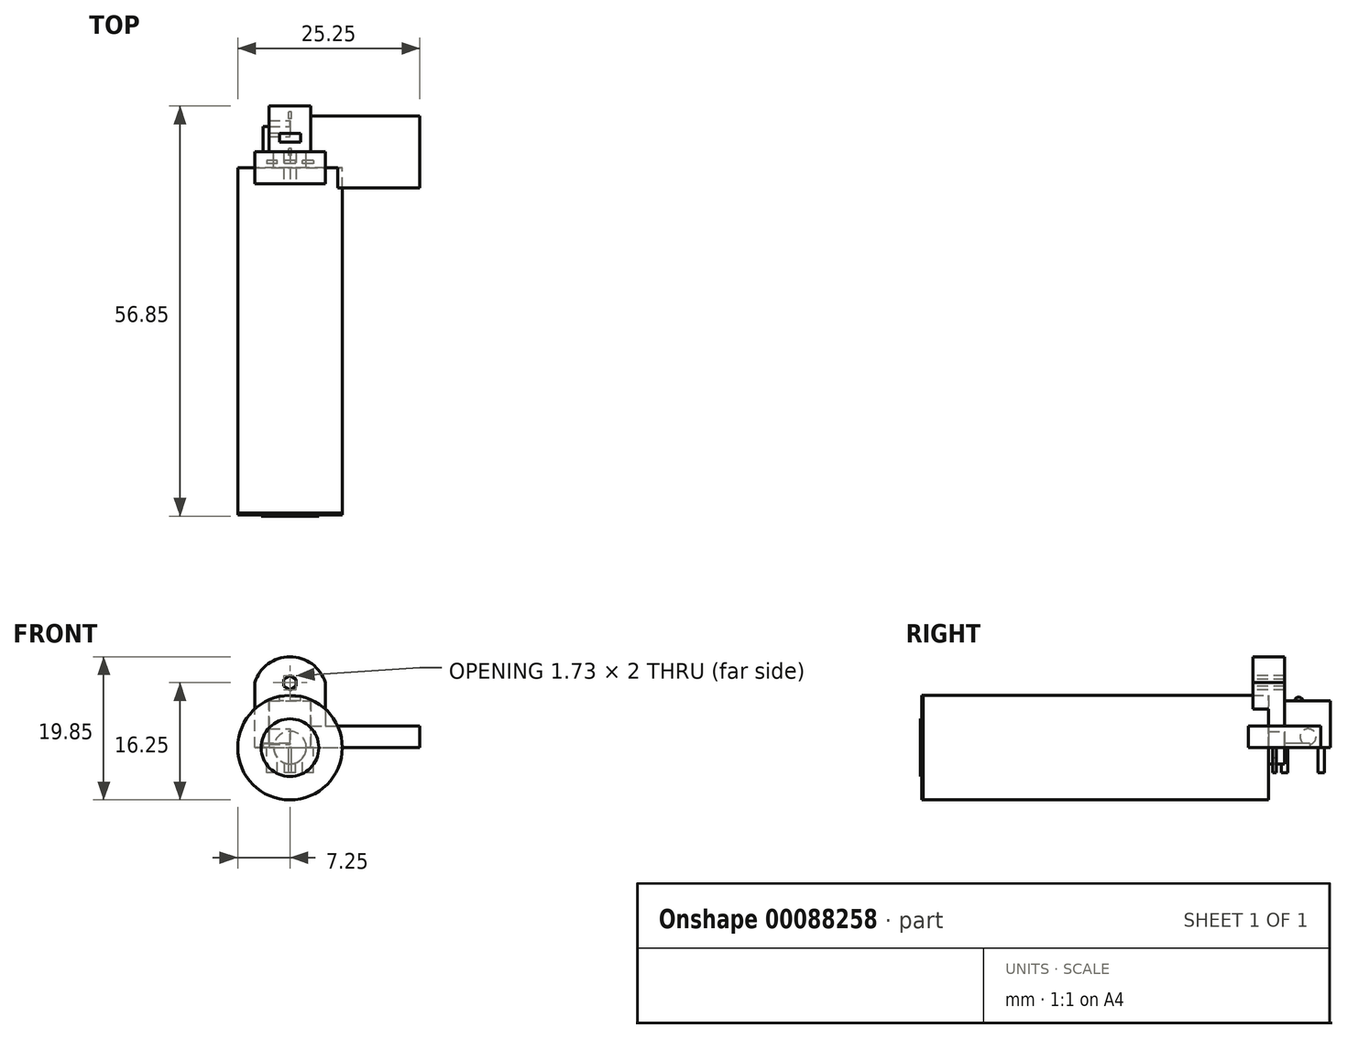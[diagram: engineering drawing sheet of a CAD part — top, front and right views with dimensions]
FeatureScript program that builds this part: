
annotation { "Feature Type Name" : "Feature", "Feature Type Description" : "" }
export const myFeature = defineFeature(function(context is Context, id is Id, definition is map)
    precondition{}
    {
        {
            var Q0;
            Q0=qCreatedBy(makeId("Top.planeOp"),FACE);
            var sketch = newSketch(context, id + "F0", { "sketchPlane" : qUnion([Q0])});
            skLineSegment(sketch, "E0.bottom", {"start": v(-2.9, 6.35) * mm, "end": v(2.9, 6.35) * mm});
            skLineSegment(sketch, "E0.top", {"start": v(-2.9, -6.35) * mm, "end": v(2.9, -6.35) * mm});
            skLineSegment(sketch, "E0.left", {"start": v(-2.9, 6.35) * mm, "end": v(-2.9, -6.35) * mm});
            skLineSegment(sketch, "E0.right", {"start": v(2.9, 6.35) * mm, "end": v(2.9, -6.35) * mm});
            skLineSegment(sketch, "E1", {"start": v(0, 9.5) * mm, "end": v(0, 7.35) * mm, "construction": true});
            skLineSegment(sketch, "E2", {"start": v(6.86, 0) * mm, "end": v(4.55, 0) * mm, "construction": true});
            skSolve(sketch);
        }
        {
            var Q0;
            Q0=qSketchRegion(id+"F0",true);
            extrude(context, id + "F1", {"entities" : qUnion([Q0]), "depth" : 6.5 * mm});
        }
        {
            var Q0;
            Q0=makeQuery(id+"F1.opExtrude","CAP_FACE",FACE,{"disambiguationData":[OSD([sQuery(id+"F0.wireOp",EDGE,"E0.bottom"),sQuery(id+"F0.wireOp",EDGE,"E0.top"),sQuery(id+"F0.wireOp",EDGE,"E0.left"),sQuery(id+"F0.wireOp",EDGE,"E0.right")])],"isStart":true});
            var sketch = newSketch(context, id + "F2", { "sketchPlane" : qUnion([Q0])});
            skLineSegment(sketch, "E3.bottom", {"start": v(0.2, 5.53) * mm, "end": v(-0.2, 5.53) * mm});
            skLineSegment(sketch, "E3.top", {"start": v(0.2, 4.63) * mm, "end": v(-0.2, 4.63) * mm});
            skLineSegment(sketch, "E3.left", {"start": v(0.2, 5.53) * mm, "end": v(0.2, 4.63) * mm});
            skLineSegment(sketch, "E3.right", {"start": v(-0.2, 5.53) * mm, "end": v(-0.2, 4.63) * mm});
            skLineSegment(sketch, "E4", {"start": v(1.77, 5.08) * mm, "end": v(0.77, 5.08) * mm, "construction": true});
            skLineSegment(sketch, "E5", {"start": v(0, -0.8) * mm, "end": v(0, -1.46) * mm, "construction": true});
            skLineSegment(sketch, "E6.0.1.0", {"start": v(-0.2, 0.45) * mm, "end": v(-0.2, -0.45) * mm});
            skLineSegment(sketch, "E6.0.1.1", {"start": v(0.2, 0.45) * mm, "end": v(0.2, -0.45) * mm});
            skLineSegment(sketch, "E6.0.1.2", {"start": v(0.2, -0.45) * mm, "end": v(-0.2, -0.45) * mm});
            skLineSegment(sketch, "E6.0.1.3", {"start": v(0.2, 0.45) * mm, "end": v(-0.2, 0.45) * mm});
            skLineSegment(sketch, "E6.0.2.0", {"start": v(-0.2, -4.63) * mm, "end": v(-0.2, -5.53) * mm});
            skLineSegment(sketch, "E6.0.2.1", {"start": v(0.2, -4.63) * mm, "end": v(0.2, -5.53) * mm});
            skLineSegment(sketch, "E6.0.2.2", {"start": v(0.2, -5.53) * mm, "end": v(-0.2, -5.53) * mm});
            skLineSegment(sketch, "E6.0.2.3", {"start": v(0.2, -4.63) * mm, "end": v(-0.2, -4.63) * mm});
            skLineSegment(sketch, "E6.direction1", {"start": v(-0.2, 4.63) * mm, "end": v(24.8, 4.63) * mm, "construction": true});
            skLineSegment(sketch, "E6.direction2", {"start": v(-0.2, 4.63) * mm, "end": v(-0.2, -0.45) * mm, "construction": true});
            skSolve(sketch);
        }
        {
            var Q0;
            Q0=qSketchRegion(id+"F2",true);
            extrude(context, id + "F3", {"entities" : qUnion([Q0]), "operationType" : NewBodyOperationType.ADD, "depth" : 3.5 * mm});
        }
        {
            var Q0;
            Q0=qCreatedBy(makeId("Right.planeOp"),FACE);
            var sketch = newSketch(context, id + "F4", { "sketchPlane" : qUnion([Q0])});
            skCircle(sketch, "E7", {"center": v(1.95, 6.4) * mm, "radius": 0.6 * mm});
            skSolve(sketch);
        }
        {
            var Q0;
            Q0=qSketchRegion(id+"F4",true);
            extrude(context, id + "F5", {"entities" : qUnion([Q0]), "operationType" : NewBodyOperationType.ADD, "endBound" : BoundingType.SYMMETRIC, "depth" : 2.9 * mm});
        }
        {
            var Q0;
            Q0=makeQuery(id+"F1.opExtrude","SWEPT_FACE",FACE,{"disambiguationData":[OSD([sQuery(id+"F0.wireOp",EDGE,"E0.right")])]});
            var sketch = newSketch(context, id + "F6", { "sketchPlane" : qUnion([Q0])});
            skCircle(sketch, "E8", {"center": v(3.25, 1.5) * mm, "radius": 1.1 * mm});
            skCircle(sketch, "E9.1.0.0", {"center": v(-3.75, 1.5) * mm, "radius": 1.1 * mm});
            skLineSegment(sketch, "E9.direction1", {"start": v(3.25, 1.5) * mm, "end": v(-3.75, 1.5) * mm, "construction": true});
            skSolve(sketch);
        }
        {
            var Q0;
            Q0=qSketchRegion(id+"F6",true);
            var Q1;
            Q1=makeQuery(id+"F1.opExtrude","SWEPT_FACE",FACE,{"disambiguationData":[OSD([sQuery(id+"F0.wireOp",EDGE,"E0.left")])]});
            extrude(context, id + "F7", {"entities" : qUnion([Q0]), "operationType" : NewBodyOperationType.REMOVE, "endBound" : BoundingType.UP_TO_SURFACE, "oppositeDirection" : true, "endBoundEntityFace" : qUnion([Q1]), "depth" : 25 * mm});
        }
        {
            var Q0;
            Q0=qCreatedBy(makeId("Top.planeOp"),FACE);
            var sketch = newSketch(context, id + "F8", { "sketchPlane" : qUnion([Q0])});
            skLineSegment(sketch, "E10", {"start": v(0, 17.78) * mm, "end": v(0, 11.28) * mm, "construction": true});
            skLineSegment(sketch, "E11", {"start": v(0, 0) * mm, "end": v(2.25, 0) * mm});
            skLineSegment(sketch, "E12", {"start": v(2.25, 0) * mm, "end": v(2.25, -2.2) * mm});
            skLineSegment(sketch, "E13", {"start": v(2.25, -2.2) * mm, "end": v(7.25, -2.2) * mm});
            skLineSegment(sketch, "E14", {"start": v(7.25, -2.2) * mm, "end": v(7.25, -50.3) * mm});
            skLineSegment(sketch, "E15", {"start": v(7.25, -50.3) * mm, "end": v(4, -50.3) * mm});
            skLineSegment(sketch, "E16", {"start": v(4, -50.3) * mm, "end": v(4, -50.5) * mm});
            skLineSegment(sketch, "E17", {"start": v(4, -50.5) * mm, "end": v(0, -50.5) * mm});
            skLineSegment(sketch, "E18", {"start": v(0, -50.5) * mm, "end": v(0, 0) * mm});
            skSolve(sketch);
        }
        {
            var Q0;
            Q0=qSketchRegion(id+"F8",true);
            var Q1;
            Q1=sQuery(id+"F8.wireOp",EDGE,"E10");
            revolve(context, id + "F9", {"entities" : qUnion([Q0]), "axis" : qUnion([Q1]), "revolveType" : RevolveType.FULL});
        }
        {
            var Q0;
            Q0=qCreatedBy(makeId("Top.planeOp"),FACE);
            var sketch = newSketch(context, id + "F10", { "sketchPlane" : qUnion([Q0])});
            skLineSegment(sketch, "E19.rect.bottom", {"start": v(0, 5) * mm, "end": v(18, 5) * mm});
            skLineSegment(sketch, "E19.rect.top", {"start": v(0, -5) * mm, "end": v(18, -5) * mm});
            skLineSegment(sketch, "E19.rect.left", {"start": v(0, 5) * mm, "end": v(0, -5) * mm});
            skLineSegment(sketch, "E19.rect.right", {"start": v(18, 5) * mm, "end": v(18, -5) * mm});
            skPoint(sketch, "E19.rect.middle", {"position": v(9, 0) * mm});
            skSolve(sketch);
        }
        {
            var Q0;
            Q0=qSketchRegion(id+"F10",true);
            extrude(context, id + "F11", {"entities" : qUnion([Q0]), "depth" : 3 * mm});
        }
        {
            var Q0;
            Q0=qCreatedBy(makeId("Top.planeOp"),FACE);
            var sketch = newSketch(context, id + "F12", { "sketchPlane" : qUnion([Q0])});
            skLineSegment(sketch, "E20.rect.bottom", {"start": v(3.75, 3.5) * mm, "end": v(-3.75, 3.5) * mm});
            skLineSegment(sketch, "E20.rect.top", {"start": v(3.75, -3.5) * mm, "end": v(-3.75, -3.5) * mm});
            skLineSegment(sketch, "E20.rect.left", {"start": v(3.75, 3.5) * mm, "end": v(3.75, -3.5) * mm});
            skLineSegment(sketch, "E20.rect.right", {"start": v(-3.75, 3.5) * mm, "end": v(-3.75, -3.5) * mm});
            skPoint(sketch, "E20.rect.middle", {"position": v(0, 0) * mm});
            skSolve(sketch);
        }
        {
            var Q0;
            Q0=qSketchRegion(id+"F12",true);
            extrude(context, id + "F13", {"entities" : qUnion([Q0]), "depth" : 0.6 * mm});
        }
        {
            var Q0;
            Q0=qCreatedBy(makeId("Front.planeOp"),FACE);
            var sketch = newSketch(context, id + "F14", { "sketchPlane" : qUnion([Q0])});
            skLineSegment(sketch, "E21", {"start": v(0, 14.23) * mm, "end": v(0, 3.29) * mm, "construction": true});
            skLineSegment(sketch, "E22", {"start": v(4.9, 0) * mm, "end": v(-4.9, 0) * mm});
            skLineSegment(sketch, "E23", {"start": v(-4.9, 0) * mm, "end": v(-4.9, 9) * mm});
            skLineSegment(sketch, "E24", {"start": v(-4.9, 9) * mm, "end": v(4.9, 9) * mm, "construction": true});
            skLineSegment(sketch, "E25", {"start": v(4.9, 9) * mm, "end": v(4.9, 0) * mm});
            skArc(sketch, "E26", {"start": v(4.9, 9) * mm, "mid": v(0, 12.6) * mm, "end": v(-4.9, 9) * mm});
            skPoint(sketch, "E27", {"position": v(0, 9) * mm});
            skSolve(sketch);
        }
        {
            var Q0;
            Q0=qSketchRegion(id+"F14",true);
            extrude(context, id + "F15", {"entities" : qUnion([Q0]), "depth" : 4.4 * mm});
        }
        {
            var Q0;
            Q0=makeQuery(id+"F15.opExtrude","CAP_FACE",FACE,{"disambiguationData":[OSD([sQuery(id+"F14.wireOp",EDGE,"E22"),sQuery(id+"F14.wireOp",EDGE,"E23"),sQuery(id+"F14.wireOp",EDGE,"E25"),sQuery(id+"F14.wireOp",EDGE,"E26")])],"isStart":false});
            var sketch = newSketch(context, id + "F16", { "sketchPlane" : qUnion([Q0])});
            skPoint(sketch, "E28.0", {"position": v(0, 9) * mm});
            skCircle(sketch, "E29.cCircle", {"center": v(0, 9) * mm, "radius": 0.87 * mm, "construction": true});
            skLineSegment(sketch, "E29.0", {"start": v(0, 10) * mm, "end": v(0.87, 9.5) * mm});
            skLineSegment(sketch, "E29.1", {"start": v(0.86, 9.5) * mm, "end": v(0.87, 8.5) * mm});
            skLineSegment(sketch, "E29.2", {"start": v(0.86, 8.5) * mm, "end": v(0, 8) * mm});
            skLineSegment(sketch, "E29.3", {"start": v(0, 8) * mm, "end": v(-0.86, 8.5) * mm});
            skLineSegment(sketch, "E29.4", {"start": v(-0.86, 8.5) * mm, "end": v(-0.87, 9.5) * mm});
            skLineSegment(sketch, "E29.5", {"start": v(-0.87, 9.5) * mm, "end": v(0, 10) * mm});
            skPoint(sketch, "E29.0.midPoint", {"position": v(0.43, 9.75) * mm});
            skSolve(sketch);
        }
        {
            var Q0;
            Q0=qSketchRegion(id+"F16",true);
            var Q1;
            Q1=makeQuery(id+"F15.opExtrude","CAP_FACE",FACE,{"disambiguationData":[OSD([sQuery(id+"F14.wireOp",EDGE,"E22"),sQuery(id+"F14.wireOp",EDGE,"E23"),sQuery(id+"F14.wireOp",EDGE,"E25"),sQuery(id+"F14.wireOp",EDGE,"E26")])],"isStart":true});
            extrude(context, id + "F17", {"entities" : qUnion([Q0]), "operationType" : NewBodyOperationType.REMOVE, "endBound" : BoundingType.UP_TO_SURFACE, "oppositeDirection" : true, "endBoundEntityFace" : qUnion([Q1]), "depth" : 25 * mm});
        }
        {
            var Q0;
            Q0=makeQuery(id+"F15.opExtrude","SWEPT_FACE",FACE,{"disambiguationData":[OSD([sQuery(id+"F14.wireOp",EDGE,"E22")])]});
            var sketch = newSketch(context, id + "F18", { "sketchPlane" : qUnion([Q0])});
            skLineSegment(sketch, "E30.0", {"start": v(4.9, 4.4) * mm, "end": v(-4.9, 4.4) * mm, "construction": true});
            skLineSegment(sketch, "E31", {"start": v(0, 4.4) * mm, "end": v(0, 0.78) * mm, "construction": true});
            skLineSegment(sketch, "E32.rect.bottom", {"start": v(0.75, 1.15) * mm, "end": v(-0.75, 1.15) * mm});
            skLineSegment(sketch, "E32.rect.top", {"start": v(0.75, 1.65) * mm, "end": v(-0.75, 1.65) * mm});
            skLineSegment(sketch, "E32.rect.left", {"start": v(0.75, 1.15) * mm, "end": v(0.75, 1.65) * mm});
            skLineSegment(sketch, "E32.rect.right", {"start": v(-0.75, 1.15) * mm, "end": v(-0.75, 1.65) * mm});
            skPoint(sketch, "E32.rect.middle", {"position": v(0, 1.4) * mm});
            skLineSegment(sketch, "E33.rect.bottom", {"start": v(3.25, 1.15) * mm, "end": v(1.75, 1.15) * mm});
            skLineSegment(sketch, "E33.rect.top", {"start": v(3.25, 1.65) * mm, "end": v(1.75, 1.65) * mm});
            skLineSegment(sketch, "E33.rect.left", {"start": v(3.25, 1.15) * mm, "end": v(3.25, 1.65) * mm});
            skLineSegment(sketch, "E33.rect.right", {"start": v(1.75, 1.15) * mm, "end": v(1.75, 1.65) * mm});
            skPoint(sketch, "E33.rect.middle", {"position": v(2.5, 1.4) * mm});
            skLineSegment(sketch, "E34.rect.bottom", {"start": v(-1.75, 1.15) * mm, "end": v(-3.25, 1.15) * mm});
            skLineSegment(sketch, "E34.rect.top", {"start": v(-1.75, 1.65) * mm, "end": v(-3.25, 1.65) * mm});
            skLineSegment(sketch, "E34.rect.left", {"start": v(-1.75, 1.15) * mm, "end": v(-1.75, 1.65) * mm});
            skLineSegment(sketch, "E34.rect.right", {"start": v(-3.25, 1.15) * mm, "end": v(-3.25, 1.65) * mm});
            skPoint(sketch, "E34.rect.middle", {"position": v(-2.5, 1.4) * mm});
            skLineSegment(sketch, "E35", {"start": v(0, 1.4) * mm, "end": v(3.46, 1.4) * mm});
            skSolve(sketch);
        }
        {
            var Q0;
            Q0=qSketchRegion(id+"F18",true);
            extrude(context, id + "F19", {"entities" : qUnion([Q0]), "operationType" : NewBodyOperationType.ADD, "depth" : 3.5 * mm});
        }
        {
            var Q0;
            Q0=qCreatedBy(makeId("Top.planeOp"),FACE);
            var sketch = newSketch(context, id + "F20", { "sketchPlane" : qUnion([Q0])});
            skLineSegment(sketch, "E36", {"start": v(0, 0) * mm, "end": v(0, -50.5) * mm});
            skLineSegment(sketch, "E37", {"start": v(0, -50.5) * mm, "end": v(4, -50.5) * mm});
            skLineSegment(sketch, "E38", {"start": v(4, -50.5) * mm, "end": v(4, -50.1) * mm});
            skLineSegment(sketch, "E39", {"start": v(4, -50.1) * mm, "end": v(7.25, -50.1) * mm});
            skLineSegment(sketch, "E40", {"start": v(7.25, -50.1) * mm, "end": v(7.25, -2.2) * mm});
            skLineSegment(sketch, "E41", {"start": v(7.25, -2.2) * mm, "end": v(2.25, -2.2) * mm});
            skLineSegment(sketch, "E42", {"start": v(2.25, -2.2) * mm, "end": v(2.25, 0) * mm});
            skLineSegment(sketch, "E43", {"start": v(2.25, 0) * mm, "end": v(0, 0) * mm});
            skSolve(sketch);
        }
        {
            var Q0;
            Q0=qSketchRegion(id+"F20",true);
            var Q1;
            Q1=sQuery(id+"F20.wireOp",EDGE,"E36");
            revolve(context, id + "F21", {"entities" : qUnion([Q0]), "axis" : qUnion([Q1]), "revolveType" : RevolveType.FULL});
        }
    });
